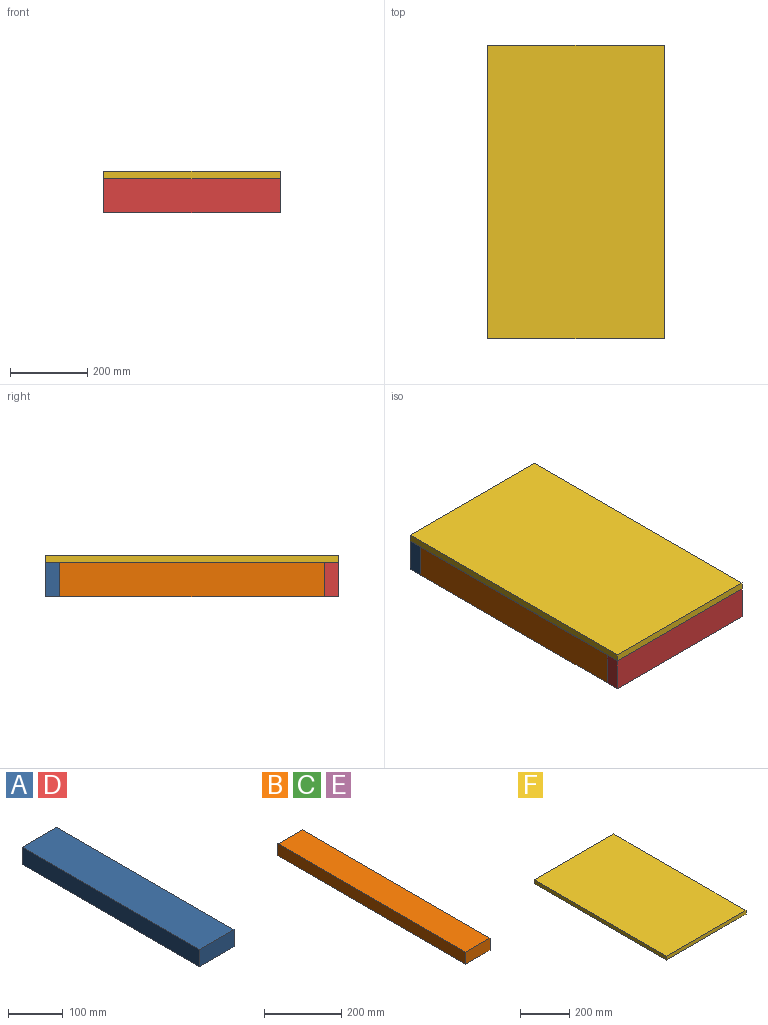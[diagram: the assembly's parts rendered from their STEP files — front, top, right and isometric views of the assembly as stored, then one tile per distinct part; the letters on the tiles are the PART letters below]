
ASSEMBLY  parts=6 mates=5
PART A: 6 faces, bbox 88.9x457.2x38.1 mm
  f0: plane 457.2x38.1mm, normal (-1,0,0), area 17419.3mm2, adj f1,f3,f4,f5
  f1: plane 457.2x88.9mm, normal (0,0,-1), area 40645.1mm2, adj f0,f2,f4,f5
  f2: plane 457.2x38.1mm, normal (1,0,0), area 17419.3mm2, adj f1,f3,f4,f5
  f3: plane 457.2x88.9mm, normal (0,0,1), area 40645.1mm2, adj f0,f2,f4,f5
  f4: plane 88.9x38.1mm, normal (0,-1,0), area 3387.1mm2, adj f0,f1,f2,f3
  f5: plane 88.9x38.1mm, normal (0,1,0), area 3387.1mm2, adj f0,f1,f2,f3
PART B: 6 faces, bbox 88.9x685.8x38.1 mm
  f0: plane 685.8x38.1mm, normal (-1,0,0), area 26129mm2, adj f1,f3,f4,f5
  f1: plane 685.8x88.9mm, normal (0,0,-1), area 60967.6mm2, adj f0,f2,f4,f5
  f2: plane 685.8x38.1mm, normal (1,0,0), area 26129mm2, adj f1,f3,f4,f5
  f3: plane 685.8x88.9mm, normal (0,0,1), area 60967.6mm2, adj f0,f2,f4,f5
  f4: plane 88.9x38.1mm, normal (0,-1,0), area 3387.1mm2, adj f0,f1,f2,f3
  f5: plane 88.9x38.1mm, normal (0,1,0), area 3387.1mm2, adj f0,f1,f2,f3
PART C: same geometry as B
PART D: same geometry as A
PART E: same geometry as B
PART F: 6 faces, bbox 457.2x762x19.1 mm
  f0: plane 762x19.05mm, normal (-1,0,0), area 14516.1mm2, adj f1,f3,f4,f5
  f1: plane 457.2x19.05mm, normal (0,-1,0), area 8709.7mm2, adj f0,f2,f4,f5
  f2: plane 762x19.05mm, normal (1,0,0), area 14516.1mm2, adj f1,f3,f4,f5
  f3: plane 457.2x19.05mm, normal (0,1,0), area 8709.7mm2, adj f0,f2,f4,f5
  f4: plane 762x457.2mm, normal (0,0,1), area 348386.4mm2, adj f0,f1,f2,f3
  f5: plane 762x457.2mm, normal (0,0,-1), area 348386.4mm2, adj f0,f1,f2,f3
PLACE A rot(axis=(-0.58,-0.58,-0.58),120deg) t=(228.6,-19.05,-88.9)mm
PLACE B rot(axis=(0.71,0,0.71),180deg) t=(-228.6,-704.85,-88.9)mm
PLACE C rot(axis=(0.71,0,0.71),180deg) t=(190.5,-704.85,-88.9)mm
PLACE D rot(axis=(-0.58,-0.58,-0.58),120deg) t=(228.6,-742.95,-88.9)mm
PLACE E rot(axis=(0.71,0,0.71),180deg) t=(-19.05,-704.85,-88.9)mm
PLACE F t=(-228.6,-742.95,0)mm
MATE fastened D.f3 <-> C.f5  axis (0,1,0) through (228.6,-704.85,0)mm
MATE fastened B.f5 <-> D.f3  axis (0,-1,0) through (-228.6,-704.85,-44.45)mm
MATE fastened A.f2 <-> F.f5  axis (0,0,1) through (0,19.05,0)mm
MATE fastened A.f1 <-> E.f4  axis (0,-1,0) through (0,-19.05,0)mm
MATE fastened A.f1 <-> B.f4  axis (0,-1,0) through (-228.6,-19.05,-44.45)mm
